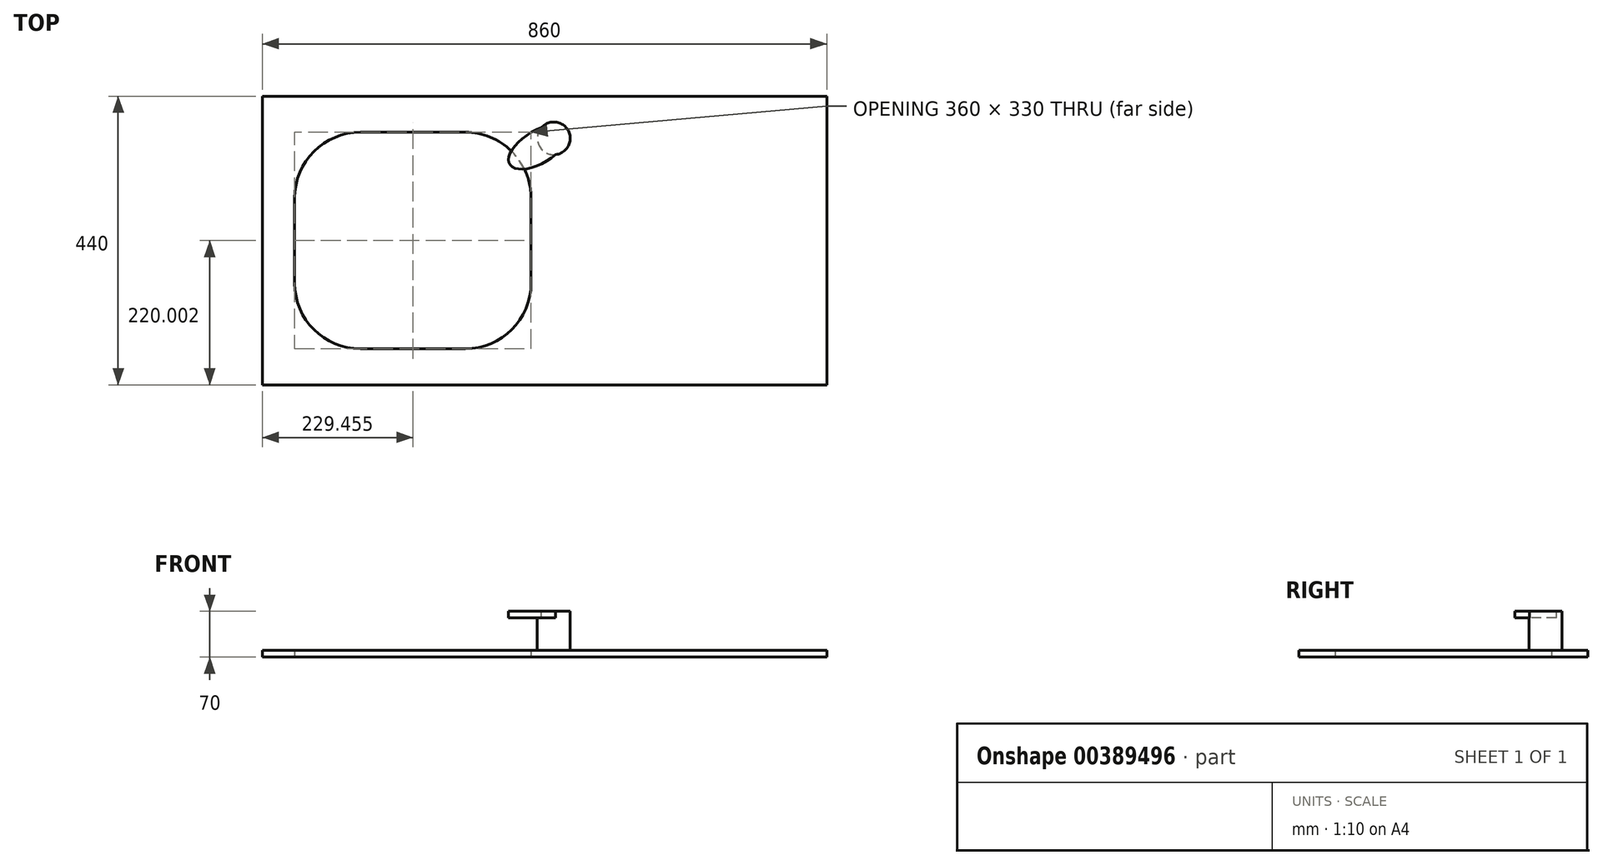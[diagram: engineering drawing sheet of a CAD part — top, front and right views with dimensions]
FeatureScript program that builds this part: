
annotation { "Feature Type Name" : "Feature", "Feature Type Description" : "" }
export const myFeature = defineFeature(function(context is Context, id is Id, definition is map)
    precondition{}
    {
        {
            var Q0;
            Q0=qCreatedBy(makeId("Top.planeOp"),FACE);
            var sketch = newSketch(context, id + "F0", { "sketchPlane" : qUnion([Q0])});
            skLineSegment(sketch, "E0.bottom", {"start": v(-411.64, 289.18) * mm, "end": v(448.36, 289.18) * mm});
            skLineSegment(sketch, "E0.top", {"start": v(-411.64, -150.82) * mm, "end": v(448.36, -150.82) * mm});
            skLineSegment(sketch, "E0.left", {"start": v(-411.64, 289.18) * mm, "end": v(-411.64, -150.82) * mm});
            skLineSegment(sketch, "E0.right", {"start": v(448.36, 289.18) * mm, "end": v(448.36, -150.82) * mm});
            skLineSegment(sketch, "E1.bottom", {"start": v(-102.19, -95.82) * mm, "end": v(-262.19, -95.82) * mm});
            skLineSegment(sketch, "E1.top", {"start": v(-102.19, 234.18) * mm, "end": v(-262.19, 234.18) * mm});
            skLineSegment(sketch, "E1.left", {"start": v(-2.19, 4.18) * mm, "end": v(-2.19, 134.18) * mm});
            skLineSegment(sketch, "E1.right", {"start": v(-362.19, 4.18) * mm, "end": v(-362.19, 134.18) * mm});
            skPoint(sketch, "E1.middle", {"position": v(-182.19, 69.18) * mm});
            skPoint(sketch, "E2.visualSharp", {"position": v(-362.19, 234.18) * mm});
            skArc(sketch, "E2.filletArc", {"start": v(-262.19, 234.18) * mm, "mid": v(-332.9, 204.9) * mm, "end": v(-362.19, 134.18) * mm});
            skPoint(sketch, "E3.visualSharp", {"position": v(-2.19, 234.18) * mm});
            skArc(sketch, "E3.filletArc", {"start": v(-2.19, 134.18) * mm, "mid": v(-31.47, 204.9) * mm, "end": v(-102.19, 234.18) * mm});
            skPoint(sketch, "E4.visualSharp", {"position": v(-2.19, -95.82) * mm});
            skArc(sketch, "E4.filletArc", {"start": v(-102.19, -95.82) * mm, "mid": v(-31.47, -66.53) * mm, "end": v(-2.19, 4.18) * mm});
            skPoint(sketch, "E5.visualSharp", {"position": v(-362.19, -95.82) * mm});
            skArc(sketch, "E5.filletArc", {"start": v(-362.19, 4.18) * mm, "mid": v(-332.9, -66.53) * mm, "end": v(-262.19, -95.82) * mm});
            skCircle(sketch, "E6", {"center": v(32.41, 224.9) * mm, "radius": 25 * mm});
            skSolve(sketch);
        }
        {
            var Q0;
            Q0=makeQuery(id+"F0.imprint","IMPRINT",FACE,{"disambiguationData":[TD([[makeQuery(id+"F0.imprint","IMPRINT",EDGE,{"derivedFrom":sQuery(id+"F0.wireOp",EDGE,"E0.bottom")}),-1.0]])]});
            extrude(context, id + "F1", {"entities" : qUnion([Q0]), "depth" : 10 * mm});
        }
        {
            var Q0;
            Q0=makeQuery(id+"F0.imprint","IMPRINT",FACE,{"disambiguationData":[TD([[makeQuery(id+"F0.imprint","IMPRINT",EDGE,{"derivedFrom":sQuery(id+"F0.wireOp",EDGE,"E6")}),1.0]])]});
            extrude(context, id + "F2", {"entities" : qUnion([Q0]), "operationType" : NewBodyOperationType.ADD, "depth" : 70 * mm});
        }
        {
            var Q0;
            Q0=makeQuery(id+"F2.opExtrude","CAP_FACE",FACE,{"disambiguationData":[OSD([sQuery(id+"F0.wireOp",EDGE,"E6")])],"isStart":false});
            var sketch = newSketch(context, id + "F3", { "sketchPlane" : qUnion([Q0])});
            skEllipse(sketch, "E7", {"center": v(9.41, 211.9) * mm, "majorRadius": 51.37 * mm, "minorRadius": 24.72 * mm, "majorAxis": v(-0.86, -0.52)});
            skFitSpline(sketch, "E8.0", {"points": [v(-27.17, 190.6) * mm, v(-26.91, 190.05) * mm, v(-26.55, 189.57) * mm, v(-25.97, 189.04) * mm, v(-25.03, 188.45) * mm, v(-23.64, 187.87) * mm, v(-21.78, 187.38) * mm, v(-19.46, 187.05) * mm, v(-17.18, 186.97) * mm, v(-15.16, 187.03) * mm, v(-13.55, 187.15) * mm, v(-11.87, 187.34) * mm, v(-9.54, 187.69) * mm, v(-6.5, 188.3) * mm, v(-2.67, 189.33) * mm, v(1.28, 190.63) * mm, v(5.32, 192.2) * mm, v(9.4, 194.02) * mm, v(12.8, 195.75) * mm, v(15.5, 197.25) * mm, v(17.52, 198.43) * mm, v(19.5, 199.66) * mm, v(22.1, 201.34) * mm, v(25.22, 203.54) * mm, v(28.74, 206.29) * mm, v(32.02, 209.12) * mm, v(35.02, 212) * mm, v(37.72, 214.9) * mm, v(39.69, 217.3) * mm, v(41.08, 219.2) * mm, v(42.04, 220.6) * mm, v(42.9, 221.96) * mm, v(43.9, 223.71) * mm, v(44.9, 225.77) * mm, v(45.7, 227.97) * mm, v(46.13, 229.84) * mm, v(46.27, 231.34) * mm, v(46.19, 232.46) * mm, v(46, 233.22) * mm, v(45.73, 233.76) * mm, v(45.37, 234.24) * mm, v(44.8, 234.77) * mm, v(43.85, 235.37) * mm, v(42.46, 235.95) * mm, v(40.6, 236.44) * mm, v(38.28, 236.76) * mm, v(36, 236.84) * mm, v(33.98, 236.78) * mm, v(32.37, 236.66) * mm, v(30.69, 236.47) * mm, v(28.36, 236.13) * mm, v(25.32, 235.51) * mm, v(21.5, 234.49) * mm, v(17.54, 233.19) * mm, v(13.5, 231.62) * mm, v(9.42, 229.8) * mm, v(6.02, 228.06) * mm, v(3.32, 226.57) * mm, v(1.3, 225.39) * mm, v(-0.69, 224.16) * mm, v(-3.27, 222.47) * mm, v(-6.4, 220.28) * mm, v(-9.92, 217.53) * mm, v(-13.2, 214.7) * mm, v(-16.2, 211.81) * mm, v(-18.9, 208.91) * mm, v(-20.86, 206.5) * mm, v(-22.26, 204.62) * mm, v(-23.22, 203.22) * mm, v(-24.07, 201.85) * mm, v(-25.08, 200.1) * mm, v(-26.07, 198.04) * mm, v(-26.87, 195.85) * mm, v(-27.31, 193.97) * mm, v(-27.45, 192.47) * mm, v(-27.37, 191.36) * mm, v(-27.17, 190.6) * mm, v(-26.91, 190.05) * mm, v(-26.55, 189.57) * mm, v(-27.17, 190.6) * mm]});
            skSolve(sketch);
        }
        {
            var Q0;
            {var subQ0=sQuery(id+"F3.wireOp",EDGE,"E7");var subQ1=makeQuery(id+"F2.opExtrude","CAP_EDGE",EDGE,{"disambiguationData":[OSD([sQuery(id+"F0.wireOp",EDGE,"E6")])],"isStart":false});var subQ2=makeQuery(id+"F3.imprint","INTERSECT",VERTEX,{"disambiguationData":[OD(0.0)],"derivedFrom":[subQ1,subQ0]});Q0=makeQuery(id+"F3.imprint","IMPRINT",FACE,{"disambiguationData":[TD([[makeQuery(id+"F3.imprint","IMPRINT",EDGE,{"disambiguationData":[TD([[subQ2,-1.0]])],"derivedFrom":subQ0}),1.0]])]});}
            extrude(context, id + "F4", {"entities" : qUnion([Q0]), "operationType" : NewBodyOperationType.ADD, "oppositeDirection" : true, "depth" : 10 * mm});
        }
    });
